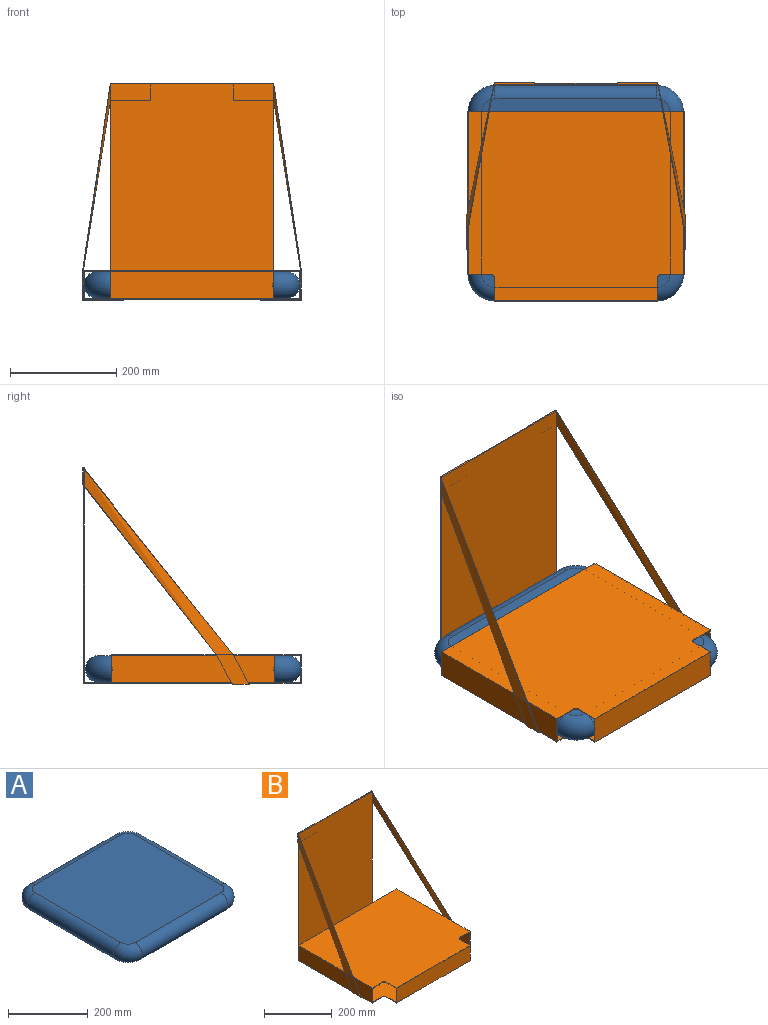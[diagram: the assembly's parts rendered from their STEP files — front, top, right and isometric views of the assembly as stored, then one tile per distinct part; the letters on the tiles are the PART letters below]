
ASSEMBLY  parts=2 mates=1
PART A: 10 faces, bbox 414.8x414.8x50.8 mm
  f0: plane 355.6x355.6mm, normal (0,0,1), area 125897.5mm2, adj f2,f3,f4,f5,f6,f7,f8,f9
  f1: plane 355.6x355.6mm, normal (0,0,-1), area 125897.5mm2, adj f2,f3,f4,f5,f6,f7,f8,f9
  f2: cylinder r=25.4mm len=304.8mm, axis (1,0,0), area 24322mm2, adj f0,f1,f3,f4
  f3: torus R=25.4mm, axis (0,0,1), area 5210.6mm2, adj f0,f1,f2,f5
  f4: torus R=25.4mm, axis (0,0,1), area 5210.6mm2, adj f0,f1,f2,f6
  f5: cylinder r=25.4mm len=304.8mm, axis (0,-1,0), area 24322mm2, adj f0,f1,f3,f7
  f6: cylinder r=25.4mm len=304.8mm, axis (0,1,0), area 24322mm2, adj f0,f1,f4,f8
  f7: torus R=25.4mm, axis (0,0,1), area 5210.6mm2, adj f0,f1,f5,f9
  f8: torus R=25.4mm, axis (0,0,1), area 5210.6mm2, adj f0,f1,f6,f9
  f9: cylinder r=25.4mm len=304.8mm, axis (-1,0,0), area 24322mm2, adj f0,f1,f7,f8
PART B: 57 faces, bbox 412.8x412.8x408 mm
  f0: plane 227.72x53.98mm, normal (-1,0,0), area 11485.3mm2, adj f6,f8,f11,f38
  f1: plane 227.72x53.98mm, normal (1,0,0), area 11485.3mm2, adj f6,f8,f11,f34
  f2: plane 307.98x53.98mm, normal (0,-1,0), area 16623mm2, adj f6,f8,f16,f18
  f3: plane 78.37x55.56mm, normal (1,0,0), area 3424.6mm2, adj f6,f8,f14,f25,f35
  f4: plane 78.37x55.56mm, normal (-1,0,0), area 3424.6mm2, adj f6,f8,f17,f29,f37
  f5: plane 406.4x357.19mm, normal (0,0,-1), area 140334.6mm2, adj f11,f14,f16,f17,f18,f20,f21,f22
  f6: plane 409.58x358.78mm, normal (0,0,1), area 141801.3mm2, adj f0,f1,f2,f3,f4,f11,f14,f16
  f7: plane 407.99x406.4mm, normal (0,0,1), area 155997mm2, adj f9,f10,f11,f12,f13,f14,f15,f16
  f8: plane 411.16x411.16mm, normal (0,0,-1), area 153115.3mm2, adj f0,f1,f2,f3,f4,f9,f10,f11
  f9: cylinder r=6.35mm len=6.35mm, axis (0,0,1), area 15.8mm2, adj f7,f8,f10,f11
  f10: plane 406.4x46.04mm, normal (-1,0,0), area 715.7mm2, adj f7,f8,f9,f40,f41,f42,f54
  f11: plane 409.58x53.98mm, normal (0,1,0), area 952.6mm2, adj f0,f1,f5,f6,f7,f8,f9,f13
  f12: plane 406.4x46.04mm, normal (1,0,0), area 715.7mm2, adj f7,f8,f13,f40,f41,f42,f51
  f13: cylinder r=6.35mm len=6.35mm, axis (0,0,1), area 15.8mm2, adj f7,f8,f11,f12
  f14: plane 53.98x44.45mm, normal (0,-1,0), area 221.8mm2, adj f3,f5,f6,f7,f8,f15,f21,f24
  f15: cylinder r=6.35mm len=6.35mm, axis (0,0,1), area 15.8mm2, adj f7,f8,f14,f16
  f16: plane 53.98x44.45mm, normal (1,0,0), area 221.8mm2, adj f2,f5,f6,f7,f8,f15,f22,f24
  f17: plane 53.98x44.45mm, normal (0,-1,0), area 221.8mm2, adj f4,f5,f6,f7,f8,f19,f20,f23
  f18: plane 53.98x44.45mm, normal (-1,0,0), area 221.8mm2, adj f2,f5,f6,f7,f8,f19,f22,f23
  f19: cylinder r=6.35mm len=6.35mm, axis (0,0,1), area 15.8mm2, adj f7,f8,f17,f18
  f20: plane 307.98x50.8mm, normal (1,0,0), area 15645.1mm2, adj f5,f7,f11,f17
  f21: plane 307.98x50.8mm, normal (-1,0,0), area 15645.1mm2, adj f5,f7,f11,f14
  f22: plane 307.98x50.8mm, normal (0,1,0), area 15645.1mm2, adj f5,f7,f16,f18
  f23: cylinder r=6.35mm len=6.35mm, axis (0,0,1), area 15.8mm2, adj f5,f6,f17,f18
  f24: cylinder r=6.35mm len=6.35mm, axis (0,0,1), area 15.8mm2, adj f5,f6,f14,f16
  f25: plane 76.2x1.59mm, normal (0,-1,0), area 121mm2, adj f3,f8,f26,f28
  f26: plane 31.75x1.59mm, normal (-1,0,0), area 50.4mm2, adj f8,f25,f27,f28
  f27: plane 76.2x1.59mm, normal (0,1,0), area 121mm2, adj f8,f26,f28,f33
  f28: plane 77.79x31.75mm, normal (0,0,-1), area 2469.8mm2, adj f25,f26,f27,f34,f35,f36
  f29: plane 76.2x1.59mm, normal (0,-1,0), area 121mm2, adj f4,f8,f31,f32
  f30: plane 77.79x1.59mm, normal (0,1,0), area 123.5mm2, adj f8,f31,f32,f39
  f31: plane 31.75x1.59mm, normal (1,0,0), area 50.4mm2, adj f8,f29,f30,f32
  f32: plane 77.79x31.75mm, normal (0,0,-1), area 2469.8mm2, adj f29,f30,f31,f37,f39
  f33: plane 1.59x0.88mm, normal (-1,0,0), area 0.7mm2, adj f8,f27,f34
  f34: plane 55.56x30.74mm, normal (0,0.88,-0.48), area 100.8mm2, adj f1,f28,f33,f36,f50
  f35: plane 55.56x30.74mm, normal (0,-0.88,0.48), area 100.8mm2, adj f3,f28,f36,f52
  f36: plane 62.49x55.56mm, normal (1,0,0), area 1764.1mm2, adj f28,f34,f35,f49
  f37: plane 55.56x30.74mm, normal (0,-0.88,0.48), area 100.8mm2, adj f4,f32,f39,f53
  f38: plane 53.98x29.86mm, normal (0,0.88,-0.48), area 97.9mm2, adj f0,f8,f39,f55
  f39: plane 62.49x55.56mm, normal (-1,0,0), area 1763.4mm2, adj f8,f30,f32,f37,f38,f56
  f40: plane 406.4x307.98mm, normal (0,1,0), area 120322.3mm2, adj f8,f10,f12,f41,f43,f44,f46,f47
  f41: plane 307.98x3.18mm, normal (0,0,1), area 730.8mm2, adj f10,f12,f40,f42,f44,f45,f47,f48
  f42: plane 404.81x307.98mm, normal (0,-1,0), area 124672.1mm2, adj f7,f10,f12,f41
  f43: plane 76.2x1.59mm, normal (0,0,-1), area 121mm2, adj f40,f44,f45,f50
  f44: plane 31.75x1.59mm, normal (-1,0,0), area 50.4mm2, adj f40,f41,f43,f45
  f45: plane 76.2x31.75mm, normal (0,1,0), area 2419.3mm2, adj f41,f43,f44,f49
  f46: plane 76.2x1.59mm, normal (0,0,-1), area 121mm2, adj f40,f47,f48,f55
  f47: plane 31.75x1.59mm, normal (1,0,0), area 50.4mm2, adj f40,f41,f46,f48
  f48: plane 76.2x31.75mm, normal (0,1,0), area 2419.3mm2, adj f41,f46,f47,f56
  f49: bspline ~352.43x283.58mm, area 9688.8mm2, adj f36,f45,f50,f52
  f50: bspline ~320.68x251.83mm, area 484.8mm2, adj f34,f43,f49,f51
  f51: bspline ~352.43x282mm, area 9658.2mm2, adj f6,f12,f50,f52
  f52: bspline ~352.43x283.58mm, area 534.3mm2, adj f35,f41,f49,f51
  f53: bspline ~352.43x283.58mm, area 534.3mm2, adj f37,f41,f54,f56
  f54: bspline ~352.43x282mm, area 9658.2mm2, adj f6,f10,f53,f55
  f55: bspline ~320.68x251.83mm, area 484.8mm2, adj f38,f46,f54,f56
  f56: bspline ~352.43x283.58mm, area 9688.8mm2, adj f39,f48,f53,f55
PLACE A t=(-0.77,-1.37,-86.15)mm
PLACE B t=(-0.41,-0.87,-87.74)mm
MATE planar A.f1 <-> B.f7  axis (0,0,-1) through (-178.57,-1.37,-86.15)mm
